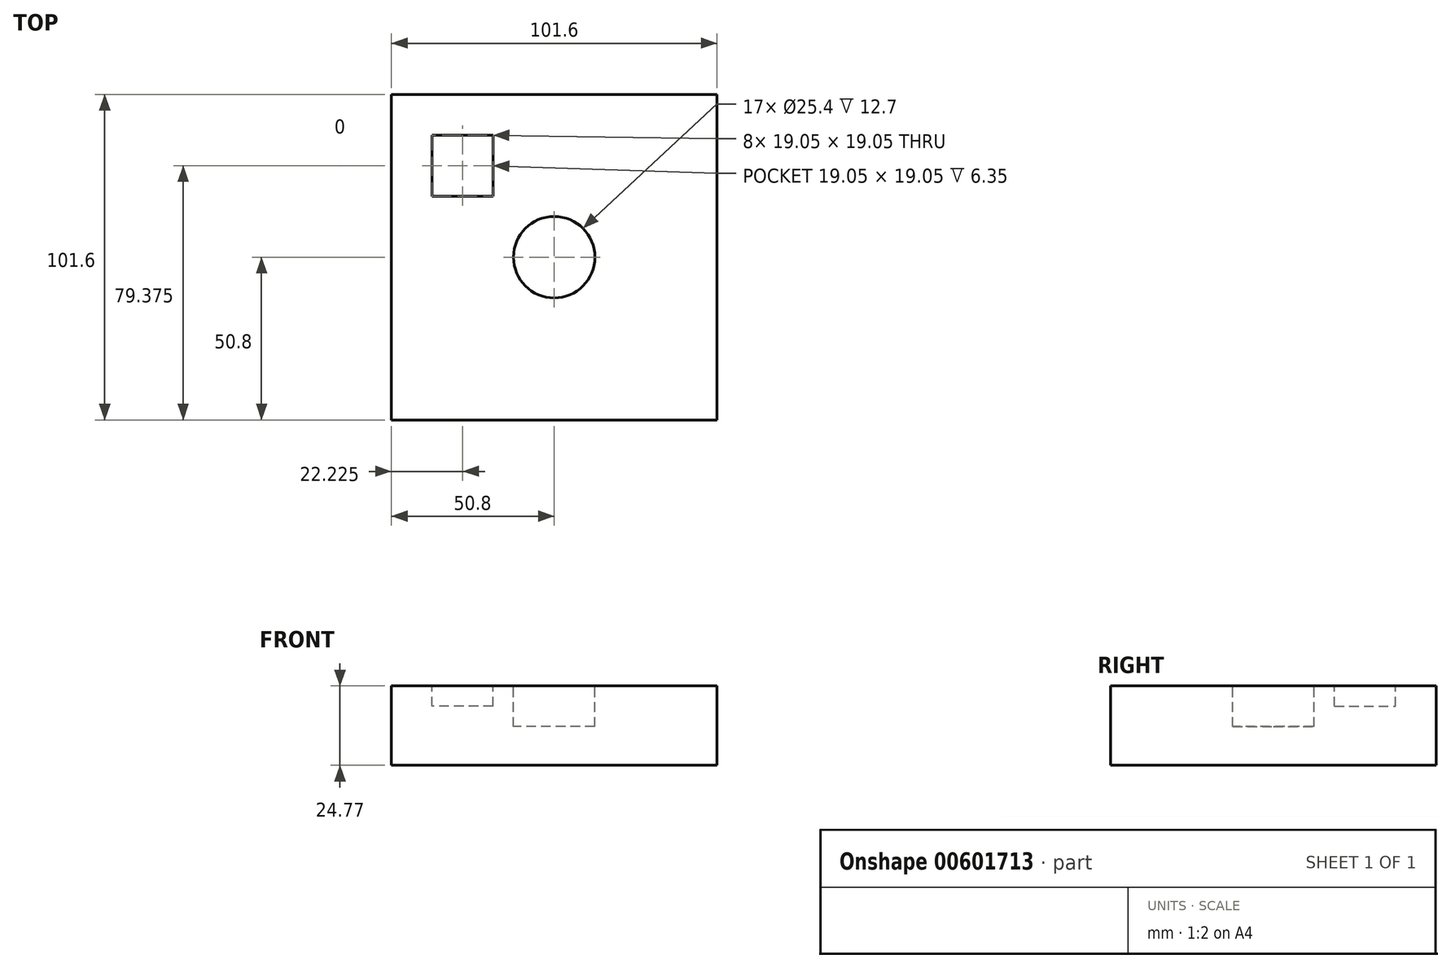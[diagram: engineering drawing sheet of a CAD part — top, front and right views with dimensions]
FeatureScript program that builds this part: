
annotation { "Feature Type Name" : "Feature", "Feature Type Description" : "" }
export const myFeature = defineFeature(function(context is Context, id is Id, definition is map)
    precondition{}
    {
        {
            var Q0;
            Q0=qCreatedBy(makeId("Top.planeOp"),FACE);
            var sketch = newSketch(context, id + "F0", { "sketchPlane" : qUnion([Q0])});
            skLineSegment(sketch, "E0.bottom", {"start": v(50.8, -50.8) * mm, "end": v(-50.8, -50.8) * mm});
            skLineSegment(sketch, "E0.top", {"start": v(50.8, 50.8) * mm, "end": v(-50.8, 50.8) * mm});
            skLineSegment(sketch, "E0.left", {"start": v(50.8, -50.8) * mm, "end": v(50.8, 50.8) * mm});
            skLineSegment(sketch, "E0.right", {"start": v(-50.8, -50.8) * mm, "end": v(-50.8, 50.8) * mm});
            skPoint(sketch, "E0.middle", {"position": v(0, 0) * mm});
            skSolve(sketch);
        }
        {
            var Q0;
            Q0=makeQuery(id+"F0.imprint","IMPRINT",FACE,{"disambiguationData":[TD([[makeQuery(id+"F0.imprint","IMPRINT",EDGE,{"derivedFrom":sQuery(id+"F0.wireOp",EDGE,"E0.bottom")}),-1.0]])]});
            extrude(context, id + "F1", {"entities" : qUnion([Q0]), "depth" : 24.76 * mm, "offsetDistance" : 25.4 * mm});
        }
        {
            var Q0;
            Q0=makeQuery(id+"F1.opExtrude","CAP_FACE",FACE,{"disambiguationData":[OSD([sQuery(id+"F0.wireOp",EDGE,"E0.bottom"),sQuery(id+"F0.wireOp",EDGE,"E0.top"),sQuery(id+"F0.wireOp",EDGE,"E0.left"),sQuery(id+"F0.wireOp",EDGE,"E0.right")])],"isStart":false});
            var sketch = newSketch(context, id + "F2", { "sketchPlane" : qUnion([Q0])});
            skCircle(sketch, "E1", {"center": v(0, 0) * mm, "radius": 12.7 * mm});
            skLineSegment(sketch, "E2.bottom", {"start": v(-19.05, 19.05) * mm, "end": v(-38.1, 19.05) * mm});
            skLineSegment(sketch, "E2.top", {"start": v(-19.05, 38.1) * mm, "end": v(-38.1, 38.1) * mm});
            skLineSegment(sketch, "E2.left", {"start": v(-19.05, 19.05) * mm, "end": v(-19.05, 38.1) * mm});
            skLineSegment(sketch, "E2.right", {"start": v(-38.1, 19.05) * mm, "end": v(-38.1, 38.1) * mm});
            skPoint(sketch, "E2.middle", {"position": v(-28.57, 28.58) * mm});
            skSolve(sketch);
        }
        {
            var Q0;
            Q0=makeQuery(id+"F2.imprint","IMPRINT",FACE,{"disambiguationData":[TD([[makeQuery(id+"F2.imprint","IMPRINT",EDGE,{"derivedFrom":sQuery(id+"F2.wireOp",EDGE,"E2.bottom")}),-1.0]])]});
            extrude(context, id + "F3", {"entities" : qUnion([Q0]), "operationType" : NewBodyOperationType.REMOVE, "oppositeDirection" : true, "depth" : 6.35 * mm, "offsetDistance" : 25.4 * mm});
        }
        {
            var Q0;
            Q0=makeQuery(id+"F2.imprint","IMPRINT",FACE,{"disambiguationData":[TD([[makeQuery(id+"F2.imprint","IMPRINT",EDGE,{"derivedFrom":sQuery(id+"F2.wireOp",EDGE,"E1")}),1.0]])]});
            extrude(context, id + "F4", {"entities" : qUnion([Q0]), "operationType" : NewBodyOperationType.REMOVE, "oppositeDirection" : true, "depth" : 12.7 * mm, "offsetDistance" : 25.4 * mm});
        }
    });
